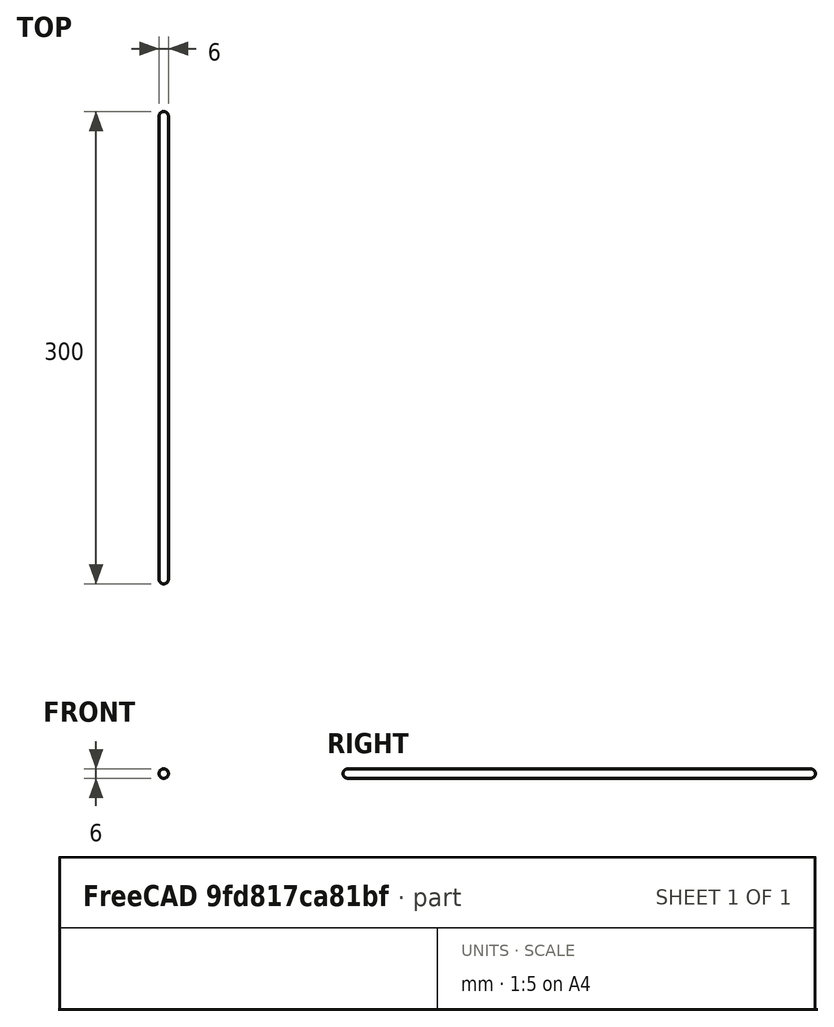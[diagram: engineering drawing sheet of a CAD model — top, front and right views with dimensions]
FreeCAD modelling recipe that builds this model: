
FCSTD DOCUMENT  (FreeCAD 0.18.4R)
Label: cup-termometer
License: All rights reserved
LicenseURL: http://en.wikipedia.org/wiki/All_rights_reserved
objects: Sketcher::SketchObject×1, PartDesign::Pad×1, PartDesign::Fillet×1, PartDesign::Body×1
note: 5 computed .brp shape members not serialized (recipe doc carries the construction recipe); baked Part::Feature solids carry a one-line shape summary decoded from their .brp

FEATURE [Sketcher::SketchObject] Sketch
  MapMode = 5
  Placement = pos=(0,0,0) rot=(1,0,0;1.5708rad)
  Support = -> [XZ_Plane]
  sketch-geometry (1):
    g0: Circle CenterX=0 CenterY=0 CenterZ=0 NormalX=0 NormalY=0 NormalZ=1 AngleXU=0 Radius=3
  constraints (2):
    c: Coincident(g0,g-1)
    c: Radius(g0) = 3
FEATURE [PartDesign::Pad] Pad
  Length = 300
  Length2 = 100
  Placement = pos=(0,0,0) rot=(1,0,0;1.5708rad)
  Profile = -> Sketch
  Reversed = true
  Type = 0
FEATURE [PartDesign::Fillet] Fillet
  Base = -> Pad [Edge3,Edge2]
  BaseFeature = -> Pad
  Placement = pos=(0,0,0) rot=(1,0,0;1.5708rad)
  Radius = 3
FEATURE [PartDesign::Body] Body
  Group = -> [Sketch,Pad,Fillet]
  Origin = -> Origin
  Tip = -> Fillet
